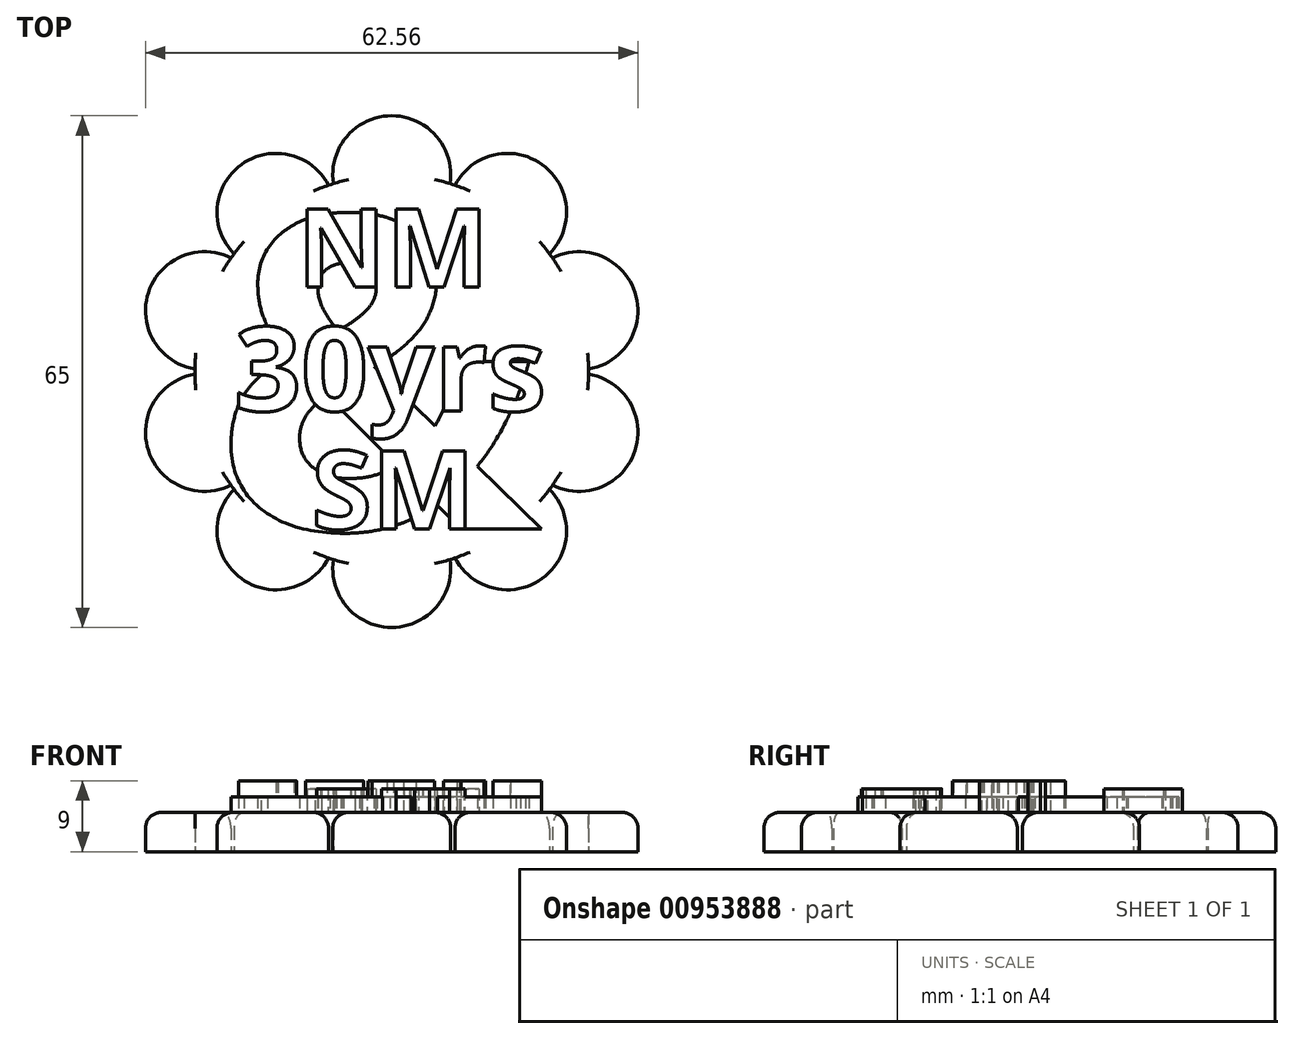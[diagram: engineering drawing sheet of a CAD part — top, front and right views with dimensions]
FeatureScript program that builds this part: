
annotation { "Feature Type Name" : "Feature", "Feature Type Description" : "" }
export const myFeature = defineFeature(function(context is Context, id is Id, definition is map)
    precondition{}
    {
        {
            var Q0;
            Q0=qCreatedBy(makeId("Top.planeOp"),FACE);
            var sketch = newSketch(context, id + "F0", { "sketchPlane" : qUnion([Q0])});
            skCircle(sketch, "E0", {"center": v(0, 0) * mm, "radius": 25 * mm});
            skCircle(sketch, "E1", {"center": v(0, 25) * mm, "radius": 7.5 * mm});
            skCircle(sketch, "E2.1.1", {"center": v(-14.7, 20.23) * mm, "radius": 7.5 * mm});
            skCircle(sketch, "E2.2.1", {"center": v(-23.78, 7.73) * mm, "radius": 7.5 * mm});
            skCircle(sketch, "E2.3.1", {"center": v(-23.78, -7.73) * mm, "radius": 7.5 * mm});
            skCircle(sketch, "E2.4.1", {"center": v(-14.7, -20.23) * mm, "radius": 7.5 * mm});
            skCircle(sketch, "E2.5.1", {"center": v(0, -25) * mm, "radius": 7.5 * mm});
            skCircle(sketch, "E2.6.1", {"center": v(14.7, -20.23) * mm, "radius": 7.5 * mm});
            skCircle(sketch, "E2.7.1", {"center": v(23.78, -7.73) * mm, "radius": 7.5 * mm});
            skCircle(sketch, "E2.8.1", {"center": v(23.78, 7.73) * mm, "radius": 7.5 * mm});
            skCircle(sketch, "E2.9.1", {"center": v(14.7, 20.23) * mm, "radius": 7.5 * mm});
            skSolve(sketch);
        }
        {
            var Q0;
            Q0 = qSketchRegion(id + "F0", true);
            extrude(context, id + "F1", {"entities" : qUnion([Q0]), "depth" : 5 * mm, "offsetDistance" : 25 * mm});
        }
        {
            var Q0;
            Q0=makeQuery(id+"F1.opExtrude","CAP_EDGE",EDGE,{"disambiguationData":[OSD([sQuery(id+"F0.wireOp",EDGE,"E2.3.1")])],"isStart":false});
            var Q1;
            Q1=makeQuery(id+"F1.opExtrude","CAP_EDGE",EDGE,{"disambiguationData":[OSD([sQuery(id+"F0.wireOp",EDGE,"E2.4.1")])],"isStart":false});
            var Q2;
            Q2=makeQuery(id+"F1.opExtrude","CAP_EDGE",EDGE,{"disambiguationData":[OSD([sQuery(id+"F0.wireOp",EDGE,"E2.5.1")])],"isStart":false});
            var Q3;
            Q3=makeQuery(id+"F1.opExtrude","CAP_EDGE",EDGE,{"disambiguationData":[OSD([sQuery(id+"F0.wireOp",EDGE,"E2.6.1")])],"isStart":false});
            var Q4;
            Q4=makeQuery(id+"F1.opExtrude","CAP_EDGE",EDGE,{"disambiguationData":[OSD([sQuery(id+"F0.wireOp",EDGE,"E2.7.1")])],"isStart":false});
            var Q5;
            Q5=makeQuery(id+"F1.opExtrude","CAP_EDGE",EDGE,{"disambiguationData":[OSD([sQuery(id+"F0.wireOp",EDGE,"E2.8.1")])],"isStart":false});
            var Q6;
            Q6=makeQuery(id+"F1.opExtrude","CAP_EDGE",EDGE,{"disambiguationData":[OSD([sQuery(id+"F0.wireOp",EDGE,"E2.9.1")])],"isStart":false});
            var Q7;
            Q7=makeQuery(id+"F1.opExtrude","CAP_EDGE",EDGE,{"disambiguationData":[OSD([sQuery(id+"F0.wireOp",EDGE,"E1")])],"isStart":false});
            var Q8;
            Q8=makeQuery(id+"F1.opExtrude","CAP_EDGE",EDGE,{"disambiguationData":[OSD([sQuery(id+"F0.wireOp",EDGE,"E2.1.1")])],"isStart":false});
            var Q9;
            Q9=makeQuery(id+"F1.opExtrude","CAP_EDGE",EDGE,{"disambiguationData":[OSD([sQuery(id+"F0.wireOp",EDGE,"E2.2.1")])],"isStart":false});
            fillet(context, id + "F2", {"entities" : qUnion([Q0, Q1, Q2, Q3, Q4, Q5, Q6, Q7, Q8, Q9]), "radius" : 2 * mm, "tangentPropagation" : true, "allowEdgeOverflow" : false});
        }
        {
            var Q0;
            Q0=makeQuery(id+"F1.opExtrude","CAP_FACE",FACE,{"disambiguationData":[OSD([sQuery(id+"F0.wireOp",EDGE,"E1"),sQuery(id+"F0.wireOp",EDGE,"E2.1.1"),sQuery(id+"F0.wireOp",EDGE,"E2.2.1"),sQuery(id+"F0.wireOp",EDGE,"E2.3.1"),sQuery(id+"F0.wireOp",EDGE,"E2.4.1"),sQuery(id+"F0.wireOp",EDGE,"E2.5.1"),sQuery(id+"F0.wireOp",EDGE,"E2.6.1"),sQuery(id+"F0.wireOp",EDGE,"E2.7.1"),sQuery(id+"F0.wireOp",EDGE,"E2.8.1"),sQuery(id+"F0.wireOp",EDGE,"E0"),sQuery(id+"F0.wireOp",EDGE,"E2.9.1")])],"isStart":false});
            var sketch = newSketch(context, id + "F3", { "sketchPlane" : qUnion([Q0])});
            skText(sketch, "E3", { "text": "30yrs", "fontName": "OpenSans-Bold.ttf"});
            skText(sketch, "E4", { "text": "NM", "fontName": "OpenSans-Bold.ttf"});
            skText(sketch, "E5", { "text": "SM", "fontName": "OpenSans-Bold.ttf"});
            skText(sketch, "E6", { "text": "&", "fontName": "OpenSans-Bold.ttf"});
            const initialGuessF3  = {"E3": [-0.02, -0.005, 1, 0, 0.01071], "E4": [-0.01202, 0.01071, 1, 0, 0.01], "E5": [-0.0102, -0.02, 1, 0, 0.01], "E6": [-0.02263, -0.02, 1, 0, 0.04]};
            skSetInitialGuess(sketch, initialGuessF3);
            skSolve(sketch);
        }
        {
            var Q0;
            Q0=makeQuery(id+"F3.imprint","IMPRINT",FACE,{"disambiguationData":[TD([[makeQuery(id+"F3.imprint","IMPRINT",EDGE,{"derivedFrom":sQuery(id+"F3.wireOp",EDGE,"E4.sketch_text.stroke-0")}),-1.0]])]});
            var Q1;
            Q1=makeQuery(id+"F3.imprint","IMPRINT",FACE,{"disambiguationData":[TD([[makeQuery(id+"F3.imprint","IMPRINT",EDGE,{"derivedFrom":sQuery(id+"F3.wireOp",EDGE,"E4.sketch_text.stroke-14")}),-1.0]])]});
            var Q2;
            Q2=makeQuery(id+"F3.imprint","IMPRINT",FACE,{"disambiguationData":[TD([[makeQuery(id+"F3.imprint","IMPRINT",EDGE,{"derivedFrom":sQuery(id+"F3.wireOp",EDGE,"E5.sketch_text.stroke-0")}),-1.0]])]});
            var Q3;
            Q3=makeQuery(id+"F3.imprint","IMPRINT",FACE,{"disambiguationData":[TD([[makeQuery(id+"F3.imprint","IMPRINT",EDGE,{"derivedFrom":sQuery(id+"F3.wireOp",EDGE,"E5.sketch_text.stroke-28")}),-1.0]])]});
            var Q4;
            {var subQ6=sQuery(id+"F3.wireOp",EDGE,"E5.sketch_text.stroke-15");Q4=makeQuery(id+"F3.imprint","IMPRINT",FACE,{"disambiguationData":[TD([[makeQuery(id+"F3.imprint","IMPRINT",EDGE,{"derivedFrom":subQ6}),-1.0]])]});}
            var Q5;
            {var subQ16=sQuery(id+"F3.wireOp",EDGE,"E5.sketch_text.stroke-29");Q5=makeQuery(id+"F3.imprint","IMPRINT",FACE,{"disambiguationData":[TD([[makeQuery(id+"F3.imprint","IMPRINT",EDGE,{"derivedFrom":subQ16}),-1.0]])]});}
            var Q6;
            {var subQ0=sQuery(id+"F3.wireOp",EDGE,"E5.sketch_text.stroke-34");var subQ1=sQuery(id+"F3.wireOp",EDGE,"E5.sketch_text.stroke-33");var subQ2=makeQuery(id+"F3.imprint","INTERSECT",VERTEX,{"derivedFrom":[subQ1,subQ0]});Q6=makeQuery(id+"F3.imprint","IMPRINT",FACE,{"disambiguationData":[TD([[makeQuery(id+"F3.imprint","IMPRINT",EDGE,{"disambiguationData":[TD([[subQ2,1.0]])],"derivedFrom":subQ1}),-1.0]])]});}
            var Q7;
            {var subQ0=sQuery(id+"F3.wireOp",EDGE,"E4.sketch_text.stroke-7");Q7=makeQuery(id+"F3.imprint","IMPRINT",FACE,{"disambiguationData":[TD([[makeQuery(id+"F3.imprint","IMPRINT",EDGE,{"derivedFrom":subQ0}),-1.0]])]});}
            var Q8;
            {var subQ15=sQuery(id+"F3.wireOp",EDGE,"E4.sketch_text.stroke-2");Q8=makeQuery(id+"F3.imprint","IMPRINT",FACE,{"disambiguationData":[TD([[makeQuery(id+"F3.imprint","IMPRINT",EDGE,{"derivedFrom":subQ15}),-1.0]])]});}
            var Q9;
            {var subQ0=sQuery(id+"F3.wireOp",EDGE,"E4.sketch_text.stroke-5");var subQ1=sQuery(id+"F3.wireOp",EDGE,"E4.sketch_text.stroke-4");var subQ2=makeQuery(id+"F3.imprint","INTERSECT",VERTEX,{"derivedFrom":[subQ1,subQ0]});Q9=makeQuery(id+"F3.imprint","IMPRINT",FACE,{"disambiguationData":[TD([[makeQuery(id+"F3.imprint","IMPRINT",EDGE,{"disambiguationData":[TD([[subQ2,1.0]])],"derivedFrom":subQ1}),-1.0]])]});}
            var Q10;
            {var subQ0=sQuery(id+"F3.wireOp",EDGE,"E4.sketch_text.stroke-11");var subQ1=sQuery(id+"F3.wireOp",EDGE,"E4.sketch_text.stroke-10");var subQ2=makeQuery(id+"F3.imprint","INTERSECT",VERTEX,{"derivedFrom":[subQ1,subQ0]});Q10=makeQuery(id+"F3.imprint","IMPRINT",FACE,{"disambiguationData":[TD([[makeQuery(id+"F3.imprint","IMPRINT",EDGE,{"disambiguationData":[TD([[subQ2,1.0]])],"derivedFrom":subQ1}),-1.0]])]});}
            var Q11;
            {var subQ0=sQuery(id+"F3.wireOp",EDGE,"E4.sketch_text.stroke-12");Q11=makeQuery(id+"F3.imprint","IMPRINT",FACE,{"disambiguationData":[TD([[makeQuery(id+"F3.imprint","IMPRINT",EDGE,{"derivedFrom":subQ0}),-1.0]])]});}
            var Q12;
            {var subQ1=sQuery(id+"F3.wireOp",EDGE,"E4.sketch_text.stroke-15");Q12=makeQuery(id+"F3.imprint","IMPRINT",FACE,{"disambiguationData":[TD([[makeQuery(id+"F3.imprint","IMPRINT",EDGE,{"derivedFrom":subQ1}),-1.0]])]});}
            var Q13;
            {var subQ6=sQuery(id+"F3.wireOp",EDGE,"E4.sketch_text.stroke-17");Q13=makeQuery(id+"F3.imprint","IMPRINT",FACE,{"disambiguationData":[TD([[makeQuery(id+"F3.imprint","IMPRINT",EDGE,{"derivedFrom":subQ6}),-1.0]])]});}
            var Q14;
            {var subQ0=sQuery(id+"F3.wireOp",EDGE,"E5.sketch_text.stroke-40");Q14=makeQuery(id+"F3.imprint","IMPRINT",FACE,{"disambiguationData":[TD([[makeQuery(id+"F3.imprint","IMPRINT",EDGE,{"derivedFrom":subQ0}),-1.0]])]});}
            var Q15;
            {var subQ0=sQuery(id+"F3.wireOp",EDGE,"E5.sketch_text.stroke-32");var subQ1=sQuery(id+"F3.wireOp",EDGE,"E5.sketch_text.stroke-31");var subQ2=makeQuery(id+"F3.imprint","INTERSECT",VERTEX,{"derivedFrom":[subQ1,subQ0]});Q15=makeQuery(id+"F3.imprint","IMPRINT",FACE,{"disambiguationData":[TD([[makeQuery(id+"F3.imprint","IMPRINT",EDGE,{"disambiguationData":[TD([[subQ2,1.0]])],"derivedFrom":subQ1}),-1.0]])]});}
            extrude(context, id + "F4", {"entities" : qUnion([Q0, Q1, Q2, Q3, Q4, Q5, Q6, Q7, Q8, Q9, Q10, Q11, Q12, Q13, Q14, Q15]), "operationType" : NewBodyOperationType.ADD, "depth" : 3 * mm, "offsetDistance" : 25 * mm});
        }
        {
            var Q0;
            Q0=makeQuery(id+"F3.imprint","IMPRINT",FACE,{"disambiguationData":[TD([[makeQuery(id+"F3.imprint","IMPRINT",EDGE,{"derivedFrom":sQuery(id+"F3.wireOp",EDGE,"E3.sketch_text.stroke-0")}),1.0]])]});
            var Q1;
            {var subQ4=sQuery(id+"F3.wireOp",EDGE,"E4.sketch_text.stroke-2");Q1=makeQuery(id+"F3.imprint","IMPRINT",FACE,{"disambiguationData":[TD([[makeQuery(id+"F3.imprint","IMPRINT",EDGE,{"derivedFrom":subQ4}),1.0]])]});}
            var Q2;
            {var subQ1=sQuery(id+"F3.wireOp",EDGE,"E6.sketch_text.stroke-10");var subQ3=sQuery(id+"F3.wireOp",EDGE,"E4.sketch_text.stroke-8");var subQ4=makeQuery(id+"F3.imprint","INTERSECT",VERTEX,{"derivedFrom":[subQ3,subQ1]});Q2=makeQuery(id+"F3.imprint","IMPRINT",FACE,{"disambiguationData":[TD([[makeQuery(id+"F3.imprint","IMPRINT",EDGE,{"disambiguationData":[TD([[subQ4,-1.0]])],"derivedFrom":subQ3}),1.0]])]});}
            var Q3;
            {var subQ54=sQuery(id+"F3.wireOp",EDGE,"E3.sketch_text.stroke-27");Q3=makeQuery(id+"F3.imprint","IMPRINT",FACE,{"disambiguationData":[TD([[makeQuery(id+"F3.imprint","IMPRINT",EDGE,{"derivedFrom":subQ54}),1.0]])]});}
            var Q4;
            {var subQ4=sQuery(id+"F3.wireOp",EDGE,"E5.sketch_text.stroke-29");Q4=makeQuery(id+"F3.imprint","IMPRINT",FACE,{"disambiguationData":[TD([[makeQuery(id+"F3.imprint","IMPRINT",EDGE,{"derivedFrom":subQ4}),1.0]])]});}
            var Q5;
            {var subQ0=sQuery(id+"F3.wireOp",EDGE,"E3.sketch_text.stroke-10");Q5=makeQuery(id+"F3.imprint","IMPRINT",FACE,{"disambiguationData":[TD([[makeQuery(id+"F3.imprint","IMPRINT",EDGE,{"derivedFrom":subQ0}),1.0]])]});}
            var Q6;
            {var subQ1=sQuery(id+"F3.wireOp",EDGE,"E5.sketch_text.stroke-42");Q6=makeQuery(id+"F3.imprint","IMPRINT",FACE,{"disambiguationData":[TD([[makeQuery(id+"F3.imprint","IMPRINT",EDGE,{"derivedFrom":subQ1}),1.0]])]});}
            var Q7;
            {var subQ6=sQuery(id+"F3.wireOp",EDGE,"E3.sketch_text.stroke-94");Q7=makeQuery(id+"F3.imprint","IMPRINT",FACE,{"disambiguationData":[TD([[makeQuery(id+"F3.imprint","IMPRINT",EDGE,{"derivedFrom":subQ6}),1.0]])]});}
            extrude(context, id + "F5", {"entities" : qUnion([Q0, Q1, Q2, Q3, Q4, Q5, Q6, Q7]), "operationType" : NewBodyOperationType.ADD, "depth" : 2 * mm, "offsetDistance" : 25 * mm});
        }
        {
            var Q0;
            {var subQ0=sQuery(id+"F3.wireOp",EDGE,"E3.sketch_text.stroke-15");Q0=makeQuery(id+"F3.imprint","IMPRINT",FACE,{"disambiguationData":[TD([[makeQuery(id+"F3.imprint","IMPRINT",EDGE,{"derivedFrom":subQ0}),-1.0]])]});}
            var Q1;
            Q1=makeQuery(id+"F3.imprint","IMPRINT",FACE,{"disambiguationData":[TD([[makeQuery(id+"F3.imprint","IMPRINT",EDGE,{"derivedFrom":sQuery(id+"F3.wireOp",EDGE,"E3.sketch_text.stroke-0")}),-1.0]])]});
            var Q2;
            {var subQ0=sQuery(id+"F3.wireOp",EDGE,"E3.sketch_text.stroke-9");var subQ1=sQuery(id+"F3.wireOp",EDGE,"E3.sketch_text.stroke-8");var subQ2=makeQuery(id+"F3.imprint","INTERSECT",VERTEX,{"derivedFrom":[subQ1,subQ0]});Q2=makeQuery(id+"F3.imprint","IMPRINT",FACE,{"disambiguationData":[TD([[makeQuery(id+"F3.imprint","IMPRINT",EDGE,{"disambiguationData":[TD([[subQ2,1.0]])],"derivedFrom":subQ1}),-1.0]])]});}
            var Q3;
            {var subQ8=sQuery(id+"F3.wireOp",EDGE,"E3.sketch_text.stroke-27");Q3=makeQuery(id+"F3.imprint","IMPRINT",FACE,{"disambiguationData":[TD([[makeQuery(id+"F3.imprint","IMPRINT",EDGE,{"derivedFrom":subQ8}),-1.0]])]});}
            var Q4;
            {var subQ0=sQuery(id+"F3.wireOp",EDGE,"E3.sketch_text.stroke-29");var subQ1=sQuery(id+"F3.wireOp",EDGE,"E3.sketch_text.stroke-28");var subQ2=makeQuery(id+"F3.imprint","INTERSECT",VERTEX,{"derivedFrom":[subQ1,subQ0]});Q4=makeQuery(id+"F3.imprint","IMPRINT",FACE,{"disambiguationData":[TD([[makeQuery(id+"F3.imprint","IMPRINT",EDGE,{"disambiguationData":[TD([[subQ2,1.0]])],"derivedFrom":subQ1}),-1.0]])]});}
            var Q5;
            {var subQ0=sQuery(id+"F3.wireOp",EDGE,"E3.sketch_text.stroke-33");var subQ1=sQuery(id+"F3.wireOp",EDGE,"E3.sketch_text.stroke-32");var subQ2=makeQuery(id+"F3.imprint","INTERSECT",VERTEX,{"derivedFrom":[subQ1,subQ0]});Q5=makeQuery(id+"F3.imprint","IMPRINT",FACE,{"disambiguationData":[TD([[makeQuery(id+"F3.imprint","IMPRINT",EDGE,{"disambiguationData":[TD([[subQ2,1.0]])],"derivedFrom":subQ1}),-1.0]])]});}
            var Q6;
            {var subQ4=sQuery(id+"F3.wireOp",EDGE,"E3.sketch_text.stroke-48");Q6=makeQuery(id+"F3.imprint","IMPRINT",FACE,{"disambiguationData":[TD([[makeQuery(id+"F3.imprint","IMPRINT",EDGE,{"derivedFrom":subQ4}),-1.0]])]});}
            var Q7;
            {var subQ1=sQuery(id+"F3.wireOp",EDGE,"E3.sketch_text.stroke-46");Q7=makeQuery(id+"F3.imprint","IMPRINT",FACE,{"disambiguationData":[TD([[makeQuery(id+"F3.imprint","IMPRINT",EDGE,{"derivedFrom":subQ1}),-1.0]])]});}
            var Q8;
            {var subQ1=sQuery(id+"F3.wireOp",EDGE,"E3.sketch_text.stroke-44");var subQ7=sQuery(id+"F3.wireOp",EDGE,"E3.sketch_text.stroke-45");var subQ8=makeQuery(id+"F3.imprint","INTERSECT",VERTEX,{"derivedFrom":[subQ1,subQ7]});Q8=makeQuery(id+"F3.imprint","IMPRINT",FACE,{"disambiguationData":[TD([[makeQuery(id+"F3.imprint","IMPRINT",EDGE,{"disambiguationData":[TD([[subQ8,1.0]])],"derivedFrom":subQ1}),-1.0]])]});}
            var Q9;
            {var subQ0=sQuery(id+"F3.wireOp",EDGE,"E3.sketch_text.stroke-43");Q9=makeQuery(id+"F3.imprint","IMPRINT",FACE,{"disambiguationData":[TD([[makeQuery(id+"F3.imprint","IMPRINT",EDGE,{"derivedFrom":subQ0}),-1.0]])]});}
            var Q10;
            {var subQ5=sQuery(id+"F3.wireOp",EDGE,"E3.sketch_text.stroke-60");Q10=makeQuery(id+"F3.imprint","IMPRINT",FACE,{"disambiguationData":[TD([[makeQuery(id+"F3.imprint","IMPRINT",EDGE,{"derivedFrom":subQ5}),-1.0]])]});}
            var Q11;
            {var subQ7=sQuery(id+"F3.wireOp",EDGE,"E3.sketch_text.stroke-62");Q11=makeQuery(id+"F3.imprint","IMPRINT",FACE,{"disambiguationData":[TD([[makeQuery(id+"F3.imprint","IMPRINT",EDGE,{"derivedFrom":subQ7}),-1.0]])]});}
            var Q12;
            {var subQ0=sQuery(id+"F3.wireOp",EDGE,"E3.sketch_text.stroke-76");Q12=makeQuery(id+"F3.imprint","IMPRINT",FACE,{"disambiguationData":[TD([[makeQuery(id+"F3.imprint","IMPRINT",EDGE,{"derivedFrom":subQ0}),-1.0]])]});}
            var Q13;
            Q13=makeQuery(id+"F3.imprint","IMPRINT",FACE,{"disambiguationData":[TD([[makeQuery(id+"F3.imprint","IMPRINT",EDGE,{"derivedFrom":sQuery(id+"F3.wireOp",EDGE,"E3.sketch_text.stroke-73")}),-1.0]])]});
            var Q14;
            {var subQ8=sQuery(id+"F3.wireOp",EDGE,"E3.sketch_text.stroke-83");Q14=makeQuery(id+"F3.imprint","IMPRINT",FACE,{"disambiguationData":[TD([[makeQuery(id+"F3.imprint","IMPRINT",EDGE,{"derivedFrom":subQ8}),-1.0]])]});}
            var Q15;
            {var subQ0=sQuery(id+"F3.wireOp",EDGE,"E3.sketch_text.stroke-88");Q15=makeQuery(id+"F3.imprint","IMPRINT",FACE,{"disambiguationData":[TD([[makeQuery(id+"F3.imprint","IMPRINT",EDGE,{"derivedFrom":subQ0}),-1.0]])]});}
            extrude(context, id + "F6", {"entities" : qUnion([Q0, Q1, Q2, Q3, Q4, Q5, Q6, Q7, Q8, Q9, Q10, Q11, Q12, Q13, Q14, Q15]), "operationType" : NewBodyOperationType.ADD, "depth" : 4 * mm, "offsetDistance" : 25 * mm});
        }
    });
